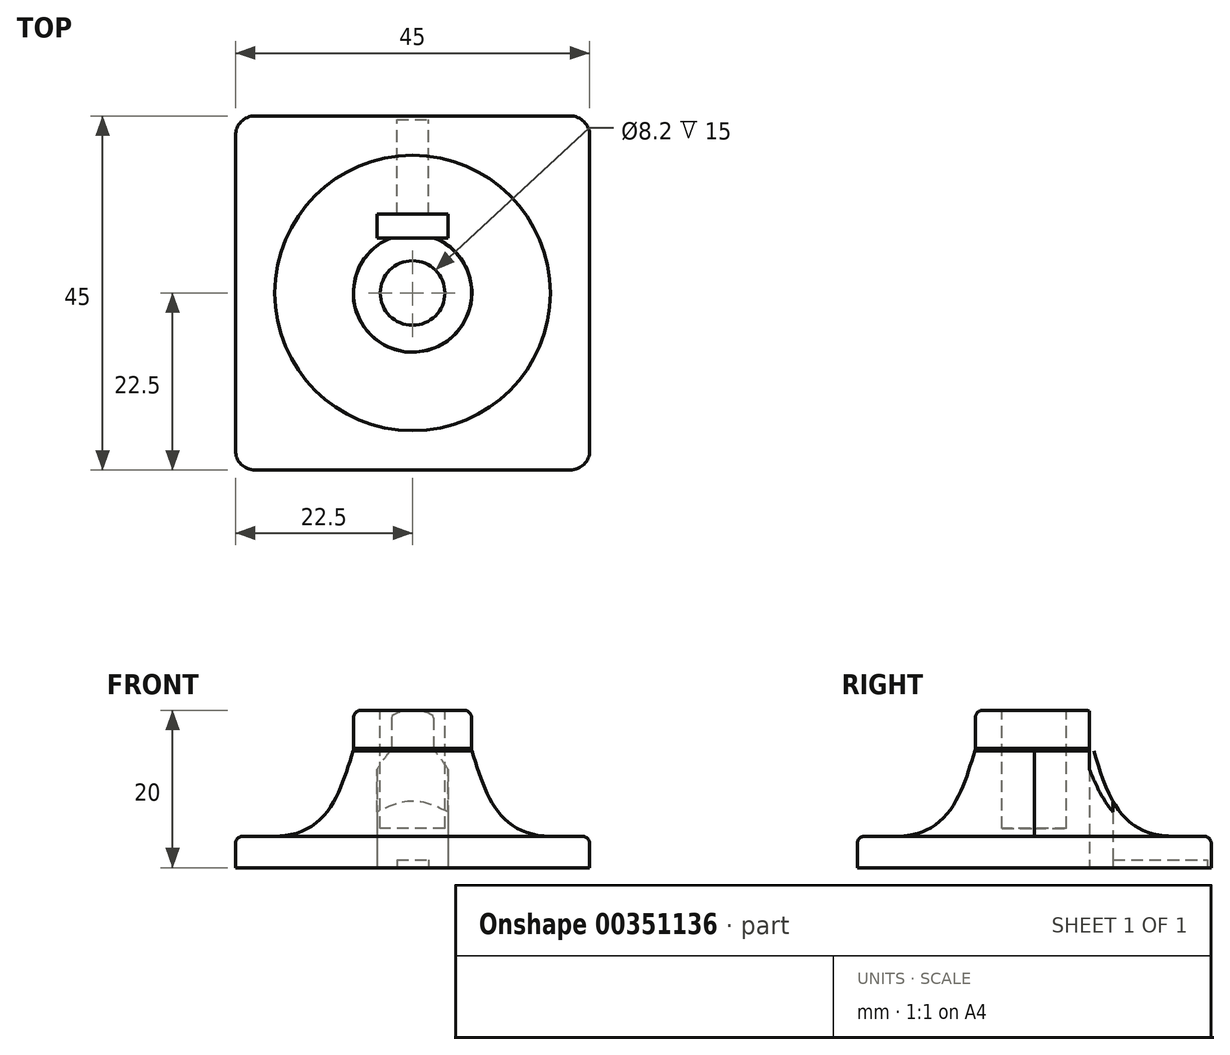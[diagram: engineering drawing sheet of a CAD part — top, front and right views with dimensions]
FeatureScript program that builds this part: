
annotation { "Feature Type Name" : "Feature", "Feature Type Description" : "" }
export const myFeature = defineFeature(function(context is Context, id is Id, definition is map)
    precondition{}
    {
        {
            var Q0;
            Q0=qCreatedBy(makeId("Top.planeOp"),FACE);
            var sketch = newSketch(context, id + "F0", { "sketchPlane" : qUnion([Q0])});
            skLineSegment(sketch, "E0.bottom", {"start": v(-20, 22.5) * mm, "end": v(20, 22.5) * mm});
            skLineSegment(sketch, "E0.top", {"start": v(-20, -22.5) * mm, "end": v(20, -22.5) * mm});
            skLineSegment(sketch, "E0.left", {"start": v(-22.5, 20) * mm, "end": v(-22.5, -20) * mm});
            skLineSegment(sketch, "E0.right", {"start": v(22.5, 20) * mm, "end": v(22.5, -20) * mm});
            skPoint(sketch, "E1.visualSharp", {"position": v(-22.5, 22.5) * mm});
            skArc(sketch, "E1.filletArc", {"start": v(-20, 22.5) * mm, "mid": v(-21.77, 21.77) * mm, "end": v(-22.5, 20) * mm});
            skPoint(sketch, "E2.visualSharp", {"position": v(22.5, 22.5) * mm});
            skArc(sketch, "E2.filletArc", {"start": v(22.5, 20) * mm, "mid": v(21.77, 21.77) * mm, "end": v(20, 22.5) * mm});
            skPoint(sketch, "E3.visualSharp", {"position": v(22.5, -22.5) * mm});
            skArc(sketch, "E3.filletArc", {"start": v(20, -22.5) * mm, "mid": v(21.77, -21.77) * mm, "end": v(22.5, -20) * mm});
            skPoint(sketch, "E4.visualSharp", {"position": v(-22.5, -22.5) * mm});
            skArc(sketch, "E4.filletArc", {"start": v(-22.5, -20) * mm, "mid": v(-21.77, -21.77) * mm, "end": v(-20, -22.5) * mm});
            skSolve(sketch);
        }
        {
            var Q0;
            Q0 = qSketchRegion(id + "F0", true);
            extrude(context, id + "F1", {"entities" : qUnion([Q0]), "depth" : 4 * mm});
        }
        {
            var Q0;
            Q0=makeQuery(id+"F1.opExtrude","CAP_EDGE",EDGE,{"disambiguationData":[OSD([sQuery(id+"F0.wireOp",EDGE,"E0.left")])],"isStart":false});
            fillet(context, id + "F2", {"entities" : qUnion([Q0]), "radius" : 1 * mm, "tangentPropagation" : true, "allowEdgeOverflow" : false});
        }
        {
            var Q0;
            Q0=qCreatedBy(makeId("Top.planeOp"),FACE);
            cPlane(context, id + "F3", {"entities" : qUnion([Q0]), "cplaneType" : CPlaneType.OFFSET, "offset" : 15 * mm, "width" : 150 * mm, "height" : 150 * mm});
        }
        {
            var Q0;
            Q0=qCreatedBy(id+"F3.planeOp",FACE);
            var sketch = newSketch(context, id + "F4", { "sketchPlane" : qUnion([Q0])});
            skCircle(sketch, "E5", {"center": v(0, 0) * mm, "radius": 7.5 * mm});
            skSolve(sketch);
        }
        {
            var Q0;
            Q0 = qSketchRegion(id + "F4", true);
            extrude(context, id + "F5", {"entities" : qUnion([Q0]), "depth" : 5 * mm});
        }
        {
            var Q0;
            Q0=makeQuery(id+"F1.opExtrude","CAP_FACE",FACE,{"disambiguationData":[OSD([sQuery(id+"F0.wireOp",EDGE,"E0.bottom"),sQuery(id+"F0.wireOp",EDGE,"E0.top"),sQuery(id+"F0.wireOp",EDGE,"E0.left"),sQuery(id+"F0.wireOp",EDGE,"E0.right"),sQuery(id+"F0.wireOp",EDGE,"E1.filletArc"),sQuery(id+"F0.wireOp",EDGE,"E2.filletArc"),sQuery(id+"F0.wireOp",EDGE,"E3.filletArc"),sQuery(id+"F0.wireOp",EDGE,"E4.filletArc")])],"isStart":false});
            var sketch = newSketch(context, id + "F6", { "sketchPlane" : qUnion([Q0])});
            skCircle(sketch, "E6", {"center": v(0, 0) * mm, "radius": 17.5 * mm});
            skSolve(sketch);
        }
        {
            var Q1;
            Q1 = qSketchRegion(id + "F6", true);
            var Q2;
            Q2 = qSketchRegion(id + "F4", true);
            loft(context, id + "F7", {"operationType" : NewBodyOperationType.ADD, "startCondition" : LoftEndDerivativeType.TANGENT_TO_PROFILE, "startMagnitude" : 2, "sheetProfilesArray" : [{ "sheetProfileEntities" : qUnion([Q1]) }, { "sheetProfileEntities" : qUnion([Q2]) }]});
        }
        {
            var Q0;
            Q0=makeQuery(id+"F5.opExtrude","CAP_FACE",FACE,{"disambiguationData":[OSD([sQuery(id+"F4.wireOp",EDGE,"E5")])],"isStart":false});
            var sketch = newSketch(context, id + "F8", { "sketchPlane" : qUnion([Q0])});
            skCircle(sketch, "E7", {"center": v(0, 0) * mm, "radius": 4.1 * mm});
            skSolve(sketch);
        }
        {
            var Q0;
            Q0 = qSketchRegion(id + "F8", true);
            extrude(context, id + "F9", {"entities" : qUnion([Q0]), "operationType" : NewBodyOperationType.REMOVE, "oppositeDirection" : true, "depth" : 15 * mm});
        }
        {
            var Q0;
            Q0=makeQuery(id+"F5.opExtrude","SWEPT_FACE",FACE,{"disambiguationData":[OSD([sQuery(id+"F4.wireOp",EDGE,"E5")])]});
            fillet(context, id + "F10", {"entities" : qUnion([Q0]), "radius" : 1 * mm, "tangentPropagation" : true, "allowEdgeOverflow" : false});
        }
        {
            var Q0;
            Q0=makeQuery(id+"F1.opExtrude","CAP_FACE",FACE,{"disambiguationData":[OSD([sQuery(id+"F0.wireOp",EDGE,"E0.bottom"),sQuery(id+"F0.wireOp",EDGE,"E0.top"),sQuery(id+"F0.wireOp",EDGE,"E0.left"),sQuery(id+"F0.wireOp",EDGE,"E0.right"),sQuery(id+"F0.wireOp",EDGE,"E1.filletArc"),sQuery(id+"F0.wireOp",EDGE,"E2.filletArc"),sQuery(id+"F0.wireOp",EDGE,"E3.filletArc"),sQuery(id+"F0.wireOp",EDGE,"E4.filletArc")])],"isStart":true});
            var sketch = newSketch(context, id + "F11", { "sketchPlane" : qUnion([Q0])});
            skLineSegment(sketch, "E8.bottom", {"start": v(-4.5, -7) * mm, "end": v(4.5, -7) * mm});
            skLineSegment(sketch, "E8.top", {"start": v(-4.5, -10) * mm, "end": v(4.5, -10) * mm});
            skLineSegment(sketch, "E8.left", {"start": v(-4.5, -7) * mm, "end": v(-4.5, -10) * mm});
            skLineSegment(sketch, "E8.right", {"start": v(4.5, -7) * mm, "end": v(4.5, -10) * mm});
            skSolve(sketch);
        }
        {
            var Q0;
            Q0 = qSketchRegion(id + "F11", true);
            extrude(context, id + "F12", {"entities" : qUnion([Q0]), "operationType" : NewBodyOperationType.REMOVE, "endBound" : BoundingType.THROUGH_ALL, "oppositeDirection" : true, "depth" : 25 * mm});
        }
        {
            var Q0;
            Q0=makeQuery(id+"F1.opExtrude","CAP_FACE",FACE,{"disambiguationData":[OSD([sQuery(id+"F0.wireOp",EDGE,"E0.bottom"),sQuery(id+"F0.wireOp",EDGE,"E0.top"),sQuery(id+"F0.wireOp",EDGE,"E0.left"),sQuery(id+"F0.wireOp",EDGE,"E0.right"),sQuery(id+"F0.wireOp",EDGE,"E1.filletArc"),sQuery(id+"F0.wireOp",EDGE,"E2.filletArc"),sQuery(id+"F0.wireOp",EDGE,"E3.filletArc"),sQuery(id+"F0.wireOp",EDGE,"E4.filletArc")])],"isStart":true});
            var sketch = newSketch(context, id + "F13", { "sketchPlane" : qUnion([Q0])});
            skLineSegment(sketch, "E9.bottom", {"start": v(-2, -10) * mm, "end": v(2, -10) * mm});
            skLineSegment(sketch, "E9.top", {"start": v(-2, -22) * mm, "end": v(2, -22) * mm});
            skLineSegment(sketch, "E9.left", {"start": v(-2, -10) * mm, "end": v(-2, -22) * mm});
            skLineSegment(sketch, "E9.right", {"start": v(2, -10) * mm, "end": v(2, -22) * mm});
            skSolve(sketch);
        }
        {
            var Q0;
            Q0 = qSketchRegion(id + "F13", true);
            extrude(context, id + "F14", {"entities" : qUnion([Q0]), "operationType" : NewBodyOperationType.REMOVE, "oppositeDirection" : true, "depth" : 1 * mm});
        }
    });
